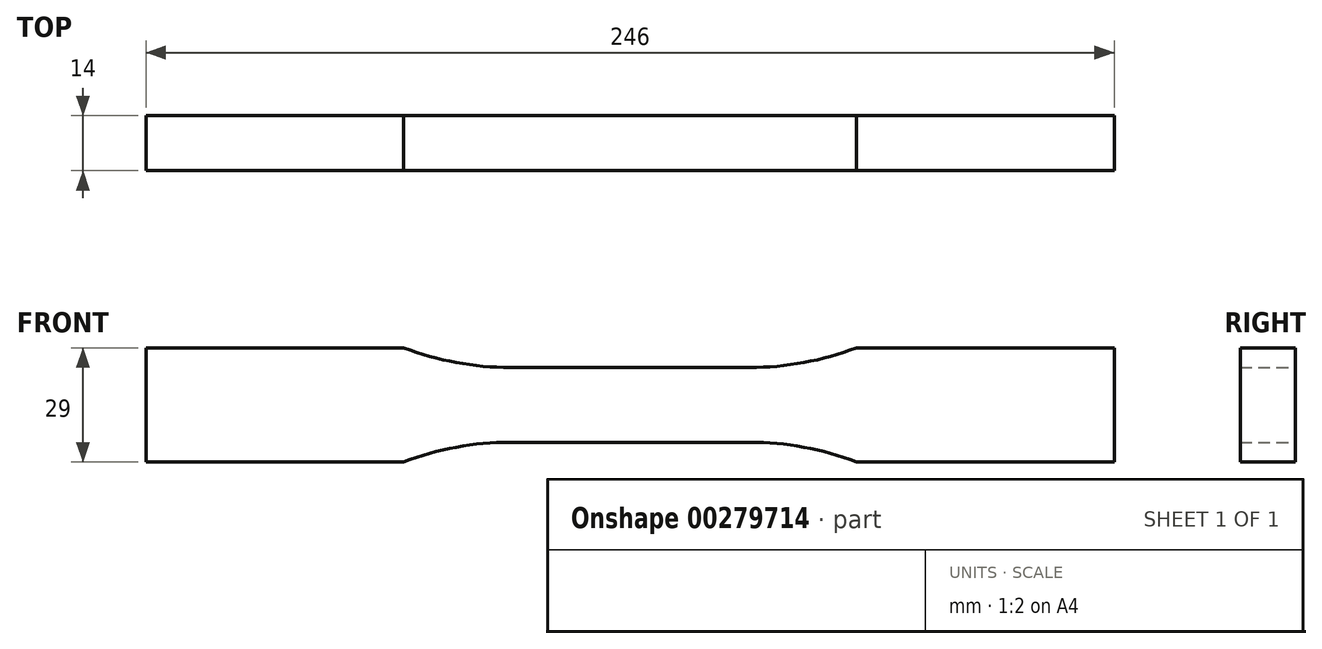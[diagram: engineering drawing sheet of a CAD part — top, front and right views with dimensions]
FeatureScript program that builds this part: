
annotation { "Feature Type Name" : "Feature", "Feature Type Description" : "" }
export const myFeature = defineFeature(function(context is Context, id is Id, definition is map)
    precondition{}
    {
        {
            var Q0;
            Q0=qCreatedBy(makeId("Front.planeOp"),FACE);
            var sketch = newSketch(context, id + "F0", { "sketchPlane" : qUnion([Q0])});
            skLineSegment(sketch, "E0", {"start": v(0, 9.5) * mm, "end": v(30.39, 9.5) * mm});
            skArc(sketch, "E1", {"start": v(30.39, 9.5) * mm, "mid": v(44.17, 10.76) * mm, "end": v(57.5, 14.5) * mm});
            skLineSegment(sketch, "E2", {"start": v(57.5, 14.5) * mm, "end": v(123, 14.5) * mm});
            skArc(sketch, "E3.MirrorCS", {"start": v(30.39, -9.5) * mm, "mid": v(44.17, -10.76) * mm, "end": v(57.5, -14.5) * mm});
            skLineSegment(sketch, "E4.MirrorCS", {"start": v(0, -9.5) * mm, "end": v(30.39, -9.5) * mm});
            skLineSegment(sketch, "E5.MirrorCS", {"start": v(57.5, -14.5) * mm, "end": v(123, -14.5) * mm});
            skLineSegment(sketch, "E6.MirrorCS", {"start": v(0, 9.5) * mm, "end": v(-30.39, 9.5) * mm});
            skArc(sketch, "E7.MirrorCS", {"start": v(-30.39, -9.5) * mm, "mid": v(-44.17, -10.76) * mm, "end": v(-57.5, -14.5) * mm});
            skArc(sketch, "E8.MirrorCS", {"start": v(-30.39, 9.5) * mm, "mid": v(-44.17, 10.76) * mm, "end": v(-57.5, 14.5) * mm});
            skLineSegment(sketch, "E9.MirrorCS", {"start": v(-57.5, 14.5) * mm, "end": v(-123, 14.5) * mm});
            skLineSegment(sketch, "E10.MirrorCS", {"start": v(0, -9.5) * mm, "end": v(-30.39, -9.5) * mm});
            skLineSegment(sketch, "E11.MirrorCS", {"start": v(-57.5, -14.5) * mm, "end": v(-123, -14.5) * mm});
            skLineSegment(sketch, "E12", {"start": v(-123, -14.5) * mm, "end": v(-123, 14.5) * mm});
            skLineSegment(sketch, "E13", {"start": v(123, -14.5) * mm, "end": v(123, 14.5) * mm});
            skSolve(sketch);
        }
        {
            var Q0;
            Q0=makeQuery(id+"F0.imprint","IMPRINT",FACE,{"disambiguationData":[TD([[makeQuery(id+"F0.imprint","IMPRINT",EDGE,{"derivedFrom":sQuery(id+"F0.wireOp",EDGE,"E0")}),-1.0]])]});
            extrude(context, id + "F1", {"entities" : qUnion([Q0]), "endBound" : BoundingType.SYMMETRIC, "depth" : 14 * mm});
        }
    });
